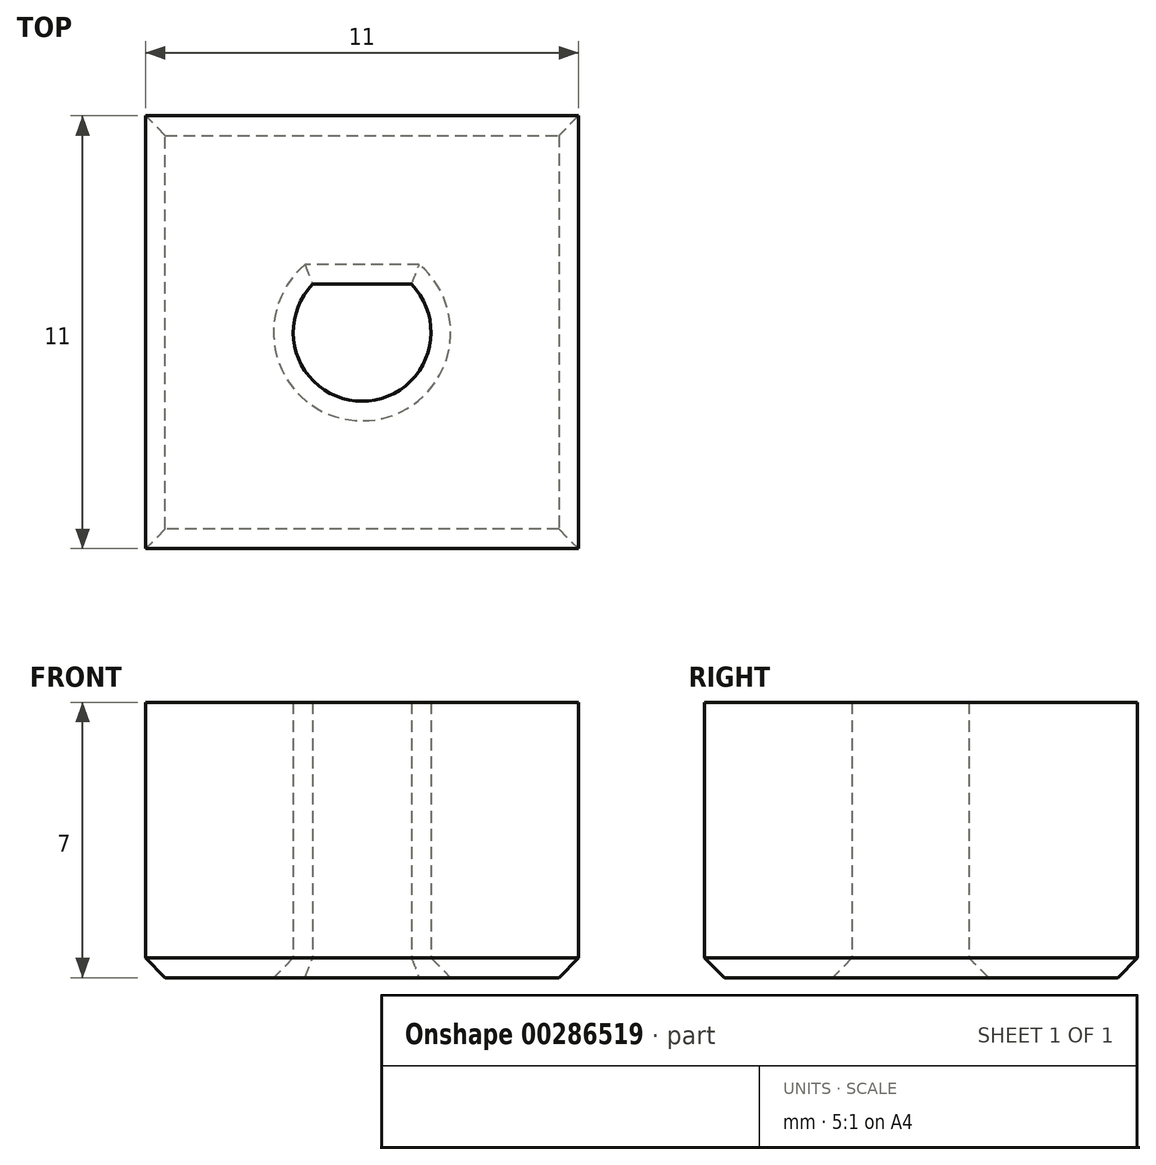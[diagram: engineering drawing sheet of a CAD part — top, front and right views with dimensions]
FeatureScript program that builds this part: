
annotation { "Feature Type Name" : "Feature", "Feature Type Description" : "" }
export const myFeature = defineFeature(function(context is Context, id is Id, definition is map)
    precondition{}
    {
        {
            var Q0;
            Q0=qCreatedBy(makeId("Top.planeOp"),FACE);
            var sketch = newSketch(context, id + "F0", { "sketchPlane" : qUnion([Q0])});
            skArc(sketch, "E0", {"start": v(-1.14, 0.97) * mm, "mid": v(0, -1.5) * mm, "end": v(1.14, 0.97) * mm});
            skLineSegment(sketch, "E1", {"start": v(-1.14, 0.97) * mm, "end": v(1.14, 0.97) * mm});
            skLineSegment(sketch, "E2.bottom", {"start": v(5.5, 5.5) * mm, "end": v(-5.5, 5.5) * mm});
            skLineSegment(sketch, "E2.top", {"start": v(5.5, -5.5) * mm, "end": v(-5.5, -5.5) * mm});
            skLineSegment(sketch, "E2.left", {"start": v(5.5, 5.5) * mm, "end": v(5.5, -5.5) * mm});
            skLineSegment(sketch, "E2.right", {"start": v(-5.5, 5.5) * mm, "end": v(-5.5, -5.5) * mm});
            skArc(sketch, "E3.0", {"start": v(-1.25, 1.22) * mm, "mid": v(0, -1.75) * mm, "end": v(1.25, 1.22) * mm});
            skLineSegment(sketch, "E3.1", {"start": v(-1.25, 1.22) * mm, "end": v(1.25, 1.22) * mm});
            skSolve(sketch);
        }
        {
            var Q0;
            Q0 = qSketchRegion(id + "F0", true);
            extrude(context, id + "F1", {"entities" : qUnion([Q0]), "depth" : 7 * mm, "offsetDistance" : 25 * mm});
        }
        {
            var Q0;
            Q0=makeQuery(id+"F1.opExtrude","CAP_FACE",FACE,{"disambiguationData":[OSD([sQuery(id+"F0.wireOp",EDGE,"E2.bottom"),sQuery(id+"F0.wireOp",EDGE,"E2.top"),sQuery(id+"F0.wireOp",EDGE,"E2.left"),sQuery(id+"F0.wireOp",EDGE,"E2.right"),sQuery(id+"F0.wireOp",EDGE,"E3.0"),sQuery(id+"F0.wireOp",EDGE,"E3.1")])],"isStart":true});
            chamfer(context, id + "F2", {"entities" : qUnion([Q0]), "width" : 0.5 * mm, "tangentPropagation" : true});
        }
    });
